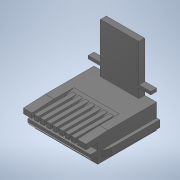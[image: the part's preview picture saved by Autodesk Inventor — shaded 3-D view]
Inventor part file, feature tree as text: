
AUTODESK INVENTOR PART (.ipt)
format: ipt  version: 2020.1 (Build 241239000, 239)  size: 506,368 bytes
history: native  units: mm
features: extrude x6, sketch x6, move_body x4, chamfer x3, mirror x1, fillet x1
ambient origin geometry x8: Origin, YZ Plane, XZ Plane, XY Plane, X Axis, Y Axis, Z Axis, Center Point
bodies: Solid1 (feature_tree)
feature tree (21):
  extrude  "Extrusion1"  Depth=12.85mm
  extrude  "Extrusion2"  Depth=0.635mm
  extrude  "Extrusion3"  Depth=1.225mm
  mirror  "Mirror1"
  chamfer  "Chamfer1"  Distance=2.54mm
  chamfer  "Chamfer2"  Distance=2.19mm
  extrude  "Extrusion4"  Depth=2.54mm
  extrude  "Extrusion5"  Depth=14.5mm TaperAngle=0.0deg
  chamfer  "Chamfer3"  Distance=4.5mm
  extrude  "Extrusion6"  Depth=0.225mm
  fillet  "Fillet1"  Radius=2.4mm
  move_body  "Move Body1"
  move_body  "Move Body2"
  move_body  "Move Body3"
  move_body  "Move Body4"
  sketch  "Sketch1"  dims[d0=5.0mm d1=12.85mm]
  sketch  "Sketch2"  dims[d4=1.4mm d5=0.635mm]
  sketch  "Sketch3"  dims[d6=0.8mm d8=1.225mm]
  sketch  "Sketch4"  dims[d9=1.755mm]
  sketch  "Sketch5"  dims[d10=0.35mm]
  sketch  "Sketch6"  dims[d11=0.45mm d12=40.0mm d14=2.54mm d15=10.0mm d17=10.0mm d20=40.0mm d22=10.0mm d23=0.35mm d24=0.45mm d26=0.82mm d27=2.19mm d30=40.0mm d32=2.54mm d33=10.0mm d35=10.0mm d37=14.5mm d38=0.0mm d39=4.5mm d40=0.225mm d41=2.4mm d42=1.235mm d43=120.0deg d44=1.225mm d45=1.315mm d46=1.5mm d47=0.6125mm d48=0.0mm d49=0.0mm d50=1.0mm d51=11.4mm d52=0.2mm d53=1.4mm d54=1.4mm d55=10.0mm d56=0.0mm d57=1.4mm d58=0.635mm d59=45.0deg d60=1.4mm d61=0.635mm d62=45.0deg d63=0.45mm d64=0.5mm d65=80.0mm d67=1.27mm d68=10.0mm d70=10.0mm d72=0.35mm d73=0.0mm d74=80.0mm d76=1.27mm d77=10.0mm d79=10.0mm d81=6.5mm d82=0.0mm d83=0.225mm d84=2.1mm d85=0.725mm d86=45.0deg d87=7.98mm d88=12.85mm d89=0.6mm d90=10.15mm d91=1.875mm d92=1.2mm d93=0.0mm d94=0.1mm d95=180.0deg d96=10.0mm d97=0.0mm d98=0.0mm d99=0.0mm d100=0.0mm d101=7.25mm d102=-10.0mm d103=0.0mm d104=0.0mm]
